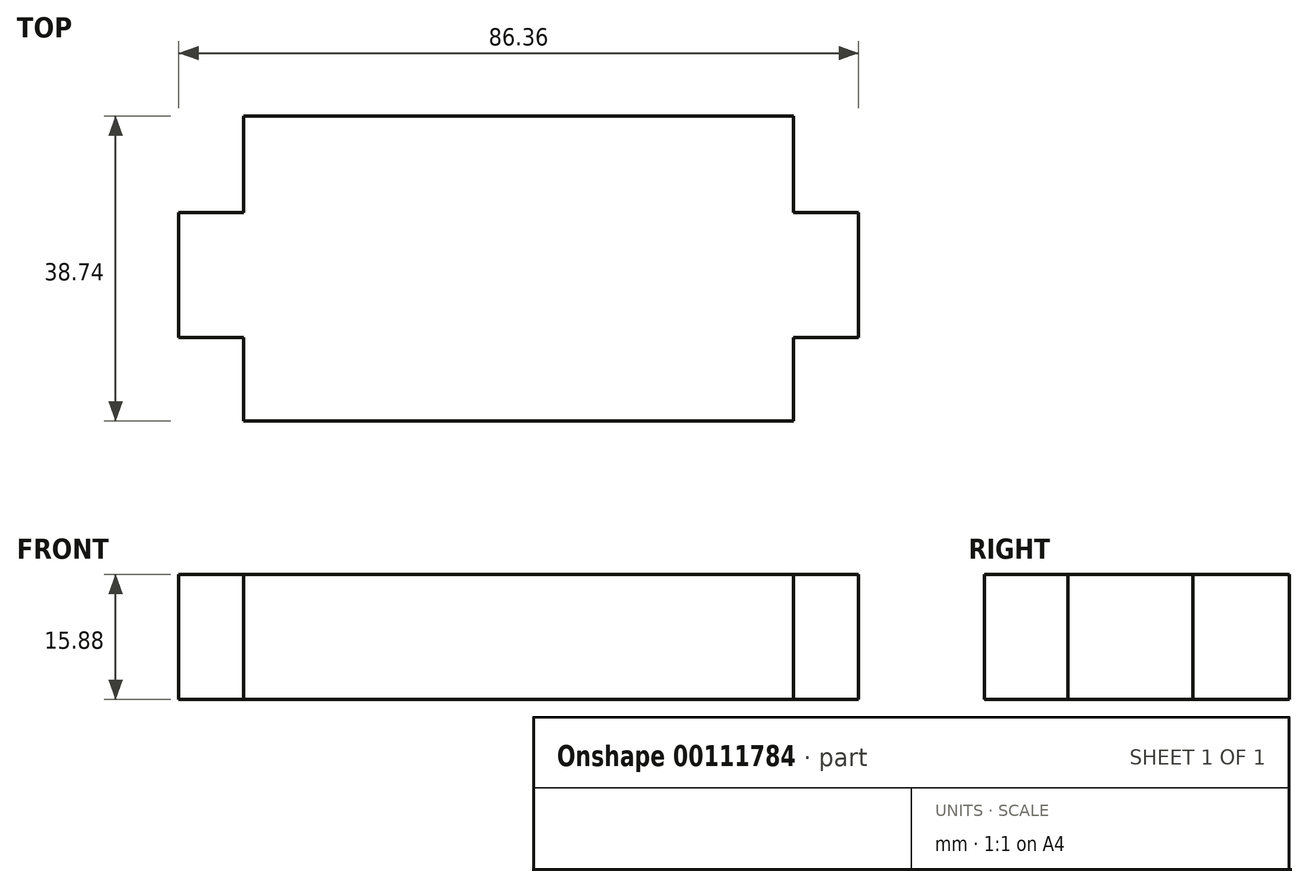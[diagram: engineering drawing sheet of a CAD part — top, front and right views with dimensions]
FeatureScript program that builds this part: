
annotation { "Feature Type Name" : "Feature", "Feature Type Description" : "" }
export const myFeature = defineFeature(function(context is Context, id is Id, definition is map)
    precondition{}
    {
        {
            var Q0;
            Q0=qCreatedBy(makeId("Top.planeOp"),FACE);
            var sketch = newSketch(context, id + "F0", { "sketchPlane" : qUnion([Q0]), "disableImprinting" : false});
            skLineSegment(sketch, "E0.bottom", {"start": v(34.93, 19.37) * mm, "end": v(-34.93, 19.37) * mm});
            skLineSegment(sketch, "E0.top", {"start": v(34.93, -19.37) * mm, "end": v(-34.93, -19.37) * mm});
            skLineSegment(sketch, "E0.left", {"start": v(34.93, 19.37) * mm, "end": v(34.93, -19.37) * mm});
            skLineSegment(sketch, "E0.right", {"start": v(-34.93, 19.37) * mm, "end": v(-34.93, -19.37) * mm});
            skPoint(sketch, "E0.middle", {"position": v(0, 0) * mm});
            skLineSegment(sketch, "E1.bottom", {"start": v(34.92, 7.13) * mm, "end": v(43.18, 7.13) * mm});
            skLineSegment(sketch, "E1.top", {"start": v(34.93, -8.74) * mm, "end": v(43.18, -8.74) * mm});
            skLineSegment(sketch, "E1.left", {"start": v(34.93, 7.13) * mm, "end": v(34.93, -8.74) * mm});
            skLineSegment(sketch, "E1.right", {"start": v(43.18, 7.13) * mm, "end": v(43.18, -8.74) * mm});
            skLineSegment(sketch, "E2.MirrorCS", {"start": v(-34.92, 7.13) * mm, "end": v(-43.18, 7.13) * mm});
            skLineSegment(sketch, "E3.MirrorCS", {"start": v(-43.18, 7.13) * mm, "end": v(-43.18, -8.74) * mm});
            skLineSegment(sketch, "E4.MirrorCS", {"start": v(-34.93, -8.74) * mm, "end": v(-43.18, -8.74) * mm});
            skLineSegment(sketch, "E5.MirrorCS", {"start": v(-34.93, 7.13) * mm, "end": v(-34.93, -8.74) * mm});
            skLineSegment(sketch, "E6", {"start": v(0, 41.39) * mm, "end": v(0, -48.18) * mm});
            skSolve(sketch);
        }
        {
            var Q0;
            Q0 = qSketchRegion(id + "F0", true);
            extrude(context, id + "F1", {"entities" : qUnion([Q0]), "oppositeDirection" : true, "depth" : 15.88 * mm});
        }
    });
